# Revit family: 23799-Deca_Cuba Quadrada de Embutir 40cm_Slim_L31040
name_source: partatom
category: Plumbing Fixtures
units: mm (PartAtom-declared; Revit-internal decimal feet)

## family parameters
Cut with Voids When Loaded = Yes
Host = Face
Part Type = Normal
Room Calculation Point = No
Round Connector Dimension = Use Radius
Shared = No

## types (1)
- L.31040.17_Branco
    Acompanha o Produto = -
    Aprovado por = quattroD
    Atendimento ao Cliente = 0800-0117073
    Composição Anel Vedação = -
    Composição Assento = -
    Composição Básica = Argila, feldspato, caulim, vidrados e corantes inorgânicos.
    Composição Componente = Liga de elastômeros e plásticos de engenharia.
    Consumo = -
    Cor Interna = branco
    Cor Principal = branco
    Cor Secundária = -
    Cores Componente = -
    Criado por = quattroD
    Código Pai = L.31040.17
    Default Elevation = 0 m
    Description = Cuba Slim Quadrada de Embutir 40cm Branco
    Diâmetro Ponto de Esgoto = 0 m
    Informações Complementares = -
    Linha = Slim
    Manufacturer = Deca
    Material = Deca_Branco
    Model = L.31040.17
    Peso Líquido (Kg) = 10.9
    Pressão máx. funcionamento = 40 MCA
    Pressão mín. Aquec. Acúmulo = -
    Pressão mín. Aquec. Passagem = -
    Pressão mín. funcionamento = 3 MCA
    Raio Ponto de Esgoto = 0 m
    Saída de Esgoto = Válvula Curta
    Segmento = Banheiro Competitivo
    Tipo de dispositivo economizador = -
    Tipo de mecanismo utilizado = -
    Tipo de rosca de entrada = -
    Tipo de rosca de saída = -
    URL = www.deca.com.br
    Vazão na Pressão máx. (L/min) = -
    Vazão na Pressão mín. (L/min) = -

## geometry (parser evidence)
native form markers: Sweep x2
no freeform markers — native parametric forms only
